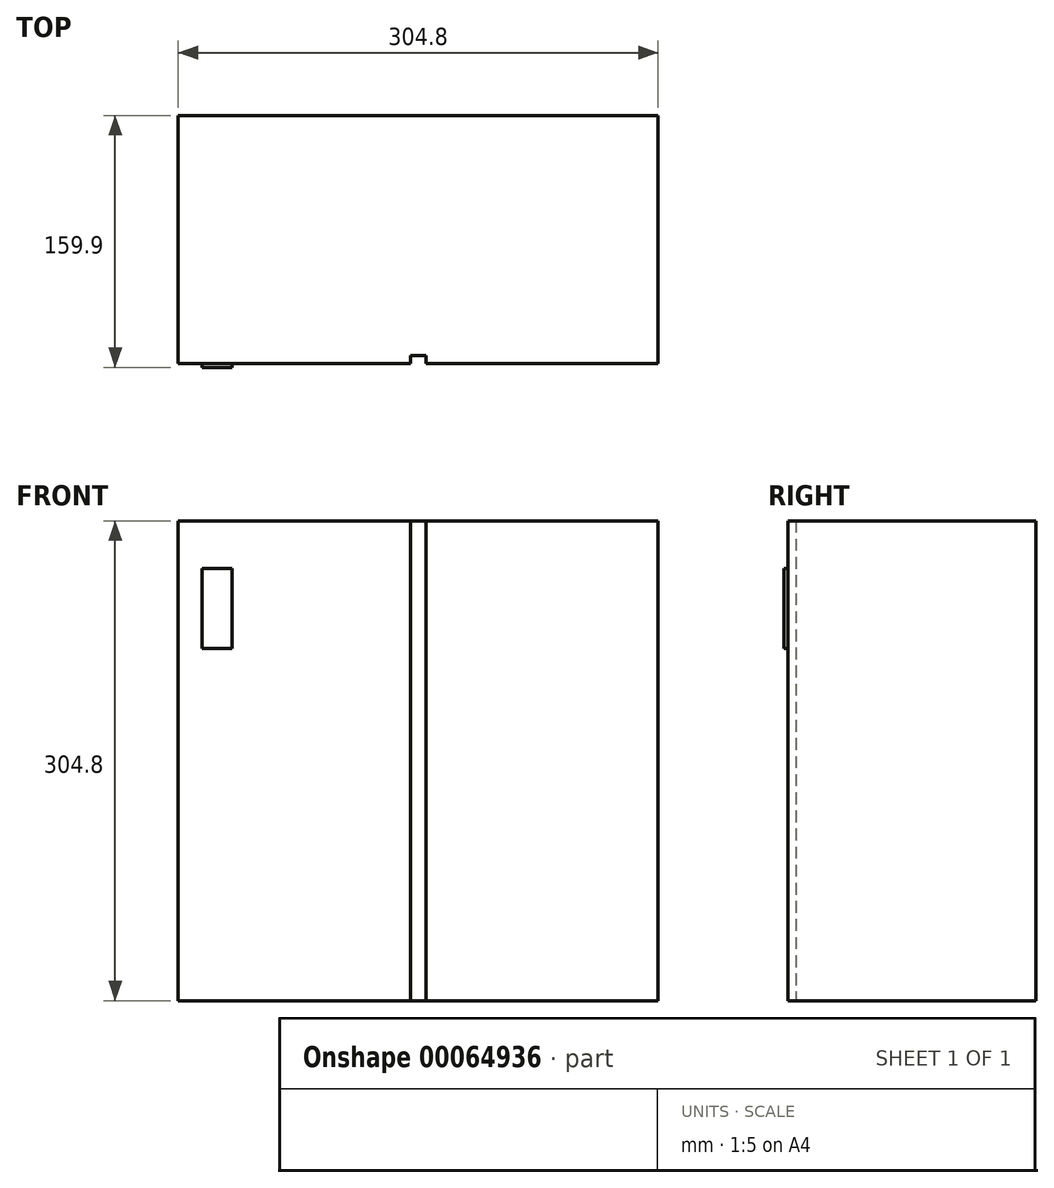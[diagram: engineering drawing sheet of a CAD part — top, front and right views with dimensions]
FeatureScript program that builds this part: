
annotation { "Feature Type Name" : "Feature", "Feature Type Description" : "" }
export const myFeature = defineFeature(function(context is Context, id is Id, definition is map)
    precondition{}
    {
        {
            var Q0;
            Q0=qCreatedBy(makeId("Top.planeOp"),FACE);
            var sketch = newSketch(context, id + "F0", { "sketchPlane" : qUnion([Q0])});
            skLineSegment(sketch, "E0", {"start": v(-155.03, 1.46) * mm, "end": v(-155.03, -150.94) * mm});
            skLineSegment(sketch, "E1", {"start": v(-155.03, -150.94) * mm, "end": v(149.77, -150.94) * mm});
            skLineSegment(sketch, "E2", {"start": v(149.77, -150.94) * mm, "end": v(149.77, 1.46) * mm});
            skLineSegment(sketch, "E3", {"start": v(149.77, 1.46) * mm, "end": v(-155.03, 1.46) * mm});
            skSolve(sketch);
        }
        {
            var Q0;
            Q0=makeQuery(id+"F0.imprint","IMPRINT",FACE,{"disambiguationData":[TD([[makeQuery(id+"F0.imprint","IMPRINT",EDGE,{"derivedFrom":sQuery(id+"F0.wireOp",EDGE,"E0")}),1.0]])]});
            extrude(context, id + "F1", {"entities" : qUnion([Q0]), "depth" : 304.8 * mm});
        }
        {
            var Q0;
            Q0=makeQuery(id+"F1.opExtrude","SWEPT_FACE",FACE,{"disambiguationData":[OSD([sQuery(id+"F0.wireOp",EDGE,"E1")])]});
            var sketch = newSketch(context, id + "F2", { "sketchPlane" : qUnion([Q0])});
            skLineSegment(sketch, "E4", {"start": v(-155.03, 304.8) * mm, "end": v(-155.03, 0) * mm});
            skLineSegment(sketch, "E5", {"start": v(-155.03, 0) * mm, "end": v(-2.63, 0) * mm});
            skLineSegment(sketch, "E6", {"start": v(-7.63, 0) * mm, "end": v(-2.63, 0) * mm});
            skLineSegment(sketch, "E7", {"start": v(-155.03, 304.8) * mm, "end": v(-7.63, 304.8) * mm});
            skLineSegment(sketch, "E8", {"start": v(-7.63, 304.8) * mm, "end": v(-7.63, 0) * mm});
            skLineSegment(sketch, "E9", {"start": v(-7.63, 304.8) * mm, "end": v(149.77, 304.8) * mm});
            skLineSegment(sketch, "E10", {"start": v(149.77, 304.8) * mm, "end": v(149.77, 0) * mm});
            skLineSegment(sketch, "E11", {"start": v(149.77, 0) * mm, "end": v(-2.63, 0) * mm});
            skLineSegment(sketch, "E12", {"start": v(2.37, 0) * mm, "end": v(-2.63, 0) * mm});
            skLineSegment(sketch, "E13", {"start": v(2.37, 0) * mm, "end": v(149.77, 0) * mm});
            skLineSegment(sketch, "E14", {"start": v(149.77, 304.8) * mm, "end": v(2.37, 304.8) * mm});
            skPoint(sketch, "E14.endSnap0", {"position": v(-2.63, 304.8) * mm});
            skLineSegment(sketch, "E15", {"start": v(2.37, 304.8) * mm, "end": v(2.37, 0) * mm});
            skLineSegment(sketch, "E16", {"start": v(-7.63, 5) * mm, "end": v(2.37, 5) * mm});
            skLineSegment(sketch, "E17", {"start": v(2.37, 5) * mm, "end": v(2.37, 0) * mm});
            skLineSegment(sketch, "E18", {"start": v(-7.63, 0) * mm, "end": v(-7.63, 5) * mm});
            skLineSegment(sketch, "E19", {"start": v(-7.63, 299.8) * mm, "end": v(2.37, 299.8) * mm});
            skLineSegment(sketch, "E20", {"start": v(2.37, 299.8) * mm, "end": v(2.37, 304.8) * mm});
            skLineSegment(sketch, "E21", {"start": v(-7.63, 304.8) * mm, "end": v(-7.63, 299.8) * mm});
            skSolve(sketch);
        }
        {
            var Q0;
            Q0=makeQuery(id+"F2.imprint","IMPRINT",FACE,{"disambiguationData":[TD([[makeQuery(id+"F2.imprint","IMPRINT",EDGE,{"derivedFrom":sQuery(id+"F2.wireOp",EDGE,"E4")}),1.0]])]});
            var Q1;
            Q1=makeQuery(id+"F2.imprint","IMPRINT",FACE,{"disambiguationData":[TD([[makeQuery(id+"F2.imprint","IMPRINT",EDGE,{"derivedFrom":sQuery(id+"F2.wireOp",EDGE,"E10")}),-1.0]])]});
            extrude(context, id + "F3", {"entities" : qUnion([Q0, Q1]), "operationType" : NewBodyOperationType.ADD, "depth" : 5 * mm});
        }
        {
            var Q0;
            Q0=makeQuery(id+"F3.opExtrude","CAP_FACE",FACE,{"disambiguationData":[OSD([sQuery(id+"F2.wireOp",EDGE,"E4"),sQuery(id+"F2.wireOp",EDGE,"E5"),sQuery(id+"F2.wireOp",EDGE,"E7"),sQuery(id+"F2.wireOp",EDGE,"E8"),sQuery(id+"F2.wireOp",EDGE,"E18"),sQuery(id+"F2.wireOp",EDGE,"E21")])],"isStart":false});
            var sketch = newSketch(context, id + "F4", { "sketchPlane" : qUnion([Q0])});
            skLineSegment(sketch, "E22.bottom", {"start": v(-140.09, 274.51) * mm, "end": v(-121.04, 274.51) * mm});
            skLineSegment(sketch, "E22.top", {"start": v(-140.09, 223.71) * mm, "end": v(-121.04, 223.71) * mm});
            skLineSegment(sketch, "E22.left", {"start": v(-140.09, 274.51) * mm, "end": v(-140.09, 223.71) * mm});
            skLineSegment(sketch, "E22.right", {"start": v(-121.04, 274.51) * mm, "end": v(-121.04, 223.71) * mm});
            skSolve(sketch);
        }
        {
            var Q0;
            Q0=makeQuery(id+"F4.imprint","IMPRINT",FACE,{"disambiguationData":[TD([[makeQuery(id+"F4.imprint","IMPRINT",EDGE,{"derivedFrom":sQuery(id+"F4.wireOp",EDGE,"E22.bottom")}),-1.0]])]});
            extrude(context, id + "F5", {"entities" : qUnion([Q0]), "operationType" : NewBodyOperationType.ADD, "depth" : 2.5 * mm});
        }
    });
